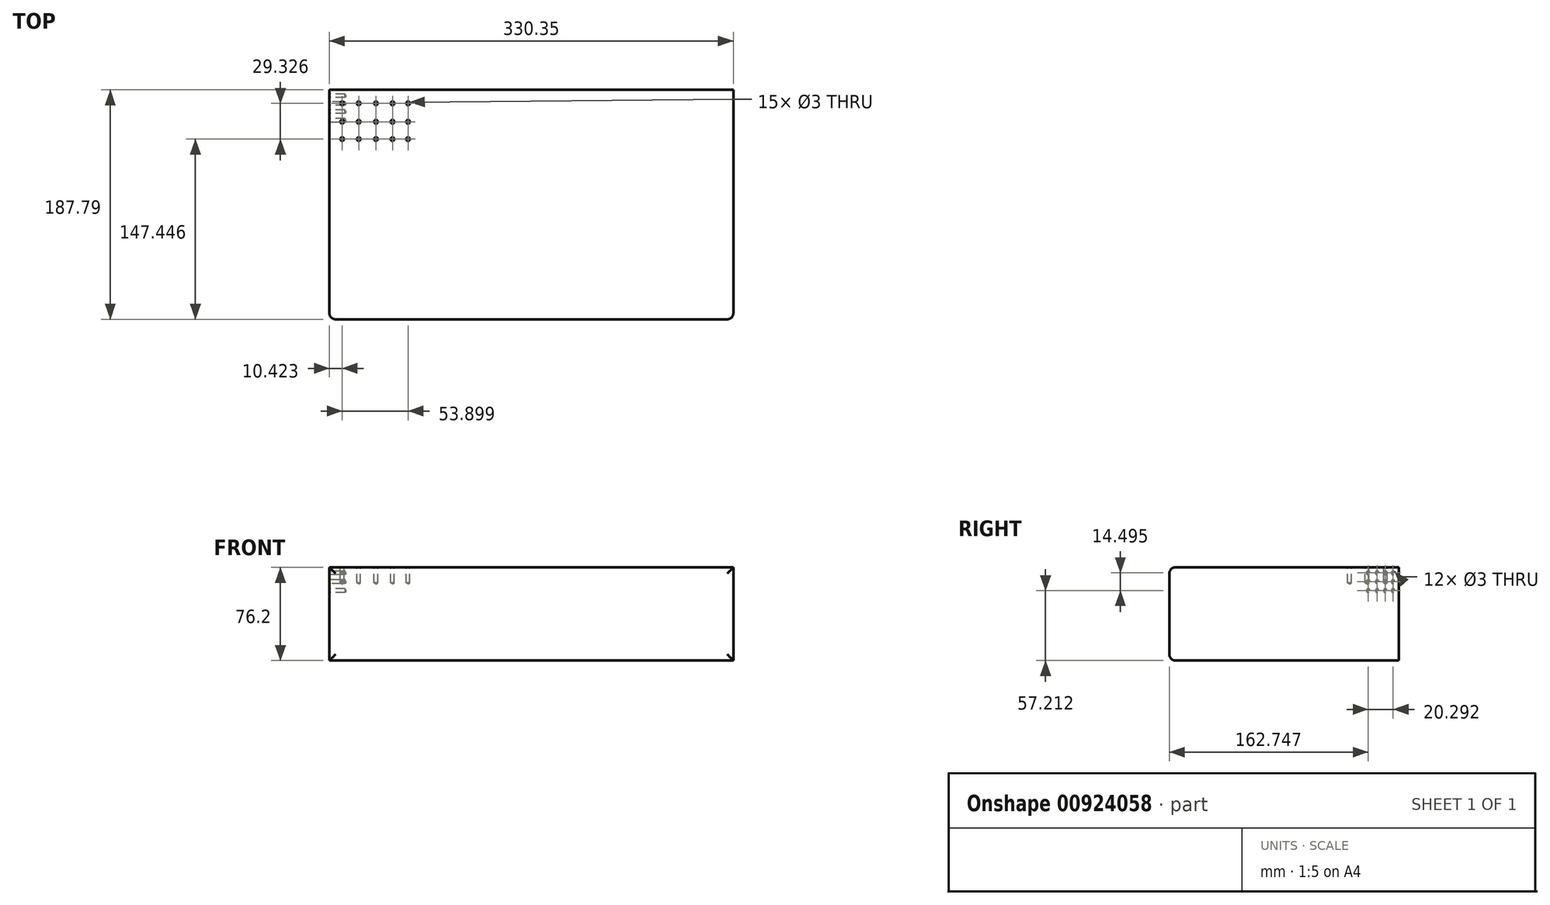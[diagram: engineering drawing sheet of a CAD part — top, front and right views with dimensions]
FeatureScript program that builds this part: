
annotation { "Feature Type Name" : "Feature", "Feature Type Description" : "" }
export const myFeature = defineFeature(function(context is Context, id is Id, definition is map)
    precondition{}
    {
        {
            var Q0;
            Q0=qCreatedBy(makeId("Top.planeOp"),FACE);
            var sketch = newSketch(context, id + "F0", { "sketchPlane" : qUnion([Q0])});
            skLineSegment(sketch, "E0.bottom", {"start": v(-154.54, 87.6) * mm, "end": v(175.81, 87.6) * mm});
            skLineSegment(sketch, "E0.top", {"start": v(-154.54, -100.2) * mm, "end": v(175.81, -100.2) * mm});
            skLineSegment(sketch, "E0.left", {"start": v(-154.54, 87.6) * mm, "end": v(-154.54, -100.2) * mm});
            skLineSegment(sketch, "E0.right", {"start": v(175.81, 87.6) * mm, "end": v(175.81, -100.2) * mm});
            skSolve(sketch);
        }
        {
            var Q0;
            Q0=makeQuery(id+"F0.imprint","IMPRINT",FACE,{"disambiguationData":[TD([[makeQuery(id+"F0.imprint","IMPRINT",EDGE,{"derivedFrom":sQuery(id+"F0.wireOp",EDGE,"E0.bottom")}),-1.0]])]});
            extrude(context, id + "F1", {"entities" : qUnion([Q0]), "oppositeDirection" : true, "depth" : 76.2 * mm, "offsetDistance" : 25.4 * mm});
        }
        {
            var Q0;
            Q0=makeQuery(id+"F1.opExtrude","CAP_EDGE",EDGE,{"disambiguationData":[OSD([sQuery(id+"F0.wireOp",EDGE,"E0.top")])],"isStart":true});
            var Q1;
            Q1=makeQuery(id+"F1.opExtrude","SWEPT_FACE",FACE,{"disambiguationData":[OSD([sQuery(id+"F0.wireOp",EDGE,"E0.top")])]});
            var Q2;
            Q2=makeQuery(id+"F1.opExtrude","CAP_EDGE",EDGE,{"disambiguationData":[OSD([sQuery(id+"F0.wireOp",EDGE,"E0.top")])],"isStart":false});
            fillet(context, id + "F2", {"entities" : qUnion([Q0, Q1, Q2]), "radius" : 5.08 * mm, "tangentPropagation" : true, "allowEdgeOverflow" : false});
        }
        {
            var Q0;
            Q0=makeQuery(id+"F1.opExtrude","CAP_FACE",FACE,{"disambiguationData":[OSD([sQuery(id+"F0.wireOp",EDGE,"E0.bottom"),sQuery(id+"F0.wireOp",EDGE,"E0.top"),sQuery(id+"F0.wireOp",EDGE,"E0.left"),sQuery(id+"F0.wireOp",EDGE,"E0.right")])],"isStart":true});
            var sketch = newSketch(context, id + "F3", { "sketchPlane" : qUnion([Q0])});
            skPoint(sketch, "E1", {"position": v(-144.12, 76.57) * mm});
            skPoint(sketch, "E2", {"position": v(-130.58, 76.57) * mm});
            skPoint(sketch, "E3", {"position": v(-130.58, 61.49) * mm});
            skPoint(sketch, "E4", {"position": v(-144.12, 61.49) * mm});
            skPoint(sketch, "E5", {"position": v(-144.12, 47.25) * mm});
            skPoint(sketch, "E6", {"position": v(-130.58, 47.25) * mm});
            skPoint(sketch, "E7", {"position": v(-116.47, 47.25) * mm});
            skPoint(sketch, "E8", {"position": v(-116.47, 61.49) * mm});
            skPoint(sketch, "E9", {"position": v(-116.47, 76.57) * mm});
            skPoint(sketch, "E10", {"position": v(-102.93, 47.25) * mm});
            skPoint(sketch, "E11", {"position": v(-102.93, 61.49) * mm});
            skPoint(sketch, "E12", {"position": v(-102.93, 76.57) * mm});
            skPoint(sketch, "E13", {"position": v(-90.22, 47.25) * mm});
            skPoint(sketch, "E14", {"position": v(-90.22, 61.49) * mm});
            skPoint(sketch, "E15", {"position": v(-90.22, 76.57) * mm});
            skSolve(sketch);
        }
        {
            var Q0;
            Q0=sQuery(id+"F3.wireOp",VERTEX,"E1");
            var Q1;
            Q1=sQuery(id+"F3.wireOp",VERTEX,"E4");
            var Q2;
            Q2=sQuery(id+"F3.wireOp",VERTEX,"E5");
            var Q3;
            Q3=sQuery(id+"F3.wireOp",VERTEX,"E6");
            var Q4;
            Q4=sQuery(id+"F3.wireOp",VERTEX,"E3");
            var Q5;
            Q5=sQuery(id+"F3.wireOp",VERTEX,"E2");
            var Q6;
            Q6=sQuery(id+"F3.wireOp",VERTEX,"E9");
            var Q7;
            Q7=sQuery(id+"F3.wireOp",VERTEX,"E8");
            var Q8;
            Q8=sQuery(id+"F3.wireOp",VERTEX,"E7");
            var Q9;
            Q9=sQuery(id+"F3.wireOp",VERTEX,"E10");
            var Q10;
            Q10=sQuery(id+"F3.wireOp",VERTEX,"E11");
            var Q11;
            Q11=sQuery(id+"F3.wireOp",VERTEX,"E12");
            var Q12;
            Q12=sQuery(id+"F3.wireOp",VERTEX,"E15");
            var Q13;
            Q13=sQuery(id+"F3.wireOp",VERTEX,"E14");
            var Q14;
            Q14=sQuery(id+"F3.wireOp",VERTEX,"E13");
            var Q15;
            Q15=makeQuery(id+"F1.opExtrude","SWEPT_BODY",BODY,{"disambiguationData":[OSD([sQuery(id+"F0.wireOp",EDGE,"E0.bottom"),sQuery(id+"F0.wireOp",EDGE,"E0.top"),sQuery(id+"F0.wireOp",EDGE,"E0.left"),sQuery(id+"F0.wireOp",EDGE,"E0.right")])]});
            hole(context, id + "F4", {"style" : HoleStyle.SIMPLE, "endStyle" : HoleEndStyle.BLIND, "standardTappedOrClearance" : lookupTablePath({ "standard" : "ISO", "size" : "3", "type" : "Drilled" }), "standardBlindInLast" : lookupTablePath({ "standard" : "ISO", "size" : "3", "type" : "Drilled" }), "holeDiameter" : 3 * mm, "majorDiameter" : 6.35 * mm, "holeDepth" : 12.7 * mm, "isTappedThrough" : true, "tappedDepth" : 12.7 * mm, "tapClearance" : 3, "locations" : qUnion([Q0, Q1, Q2, Q3, Q4, Q5, Q6, Q7, Q8, Q9, Q10, Q11, Q12, Q13, Q14]), "scope" : qUnion([Q15])});
        }
        {
            var Q0;
            Q0=makeQuery(id+"F1.opExtrude","SWEPT_FACE",FACE,{"disambiguationData":[OSD([sQuery(id+"F0.wireOp",EDGE,"E0.left")])]});
            var sketch = newSketch(context, id + "F5", { "sketchPlane" : qUnion([Q0])});
            skPoint(sketch, "E16", {"position": v(-82.84, -4.5) * mm});
            skPoint(sketch, "E17", {"position": v(-76.46, -4.5) * mm});
            skPoint(sketch, "E18", {"position": v(-69.8, -4.5) * mm});
            skPoint(sketch, "E19", {"position": v(-62.55, -4.5) * mm});
            skPoint(sketch, "E20", {"position": v(-62.55, -11.74) * mm});
            skPoint(sketch, "E21", {"position": v(-69.8, -11.74) * mm});
            skPoint(sketch, "E22", {"position": v(-76.46, -11.74) * mm});
            skPoint(sketch, "E23", {"position": v(-82.84, -11.74) * mm});
            skPoint(sketch, "E24", {"position": v(-82.84, -18.99) * mm});
            skPoint(sketch, "E25", {"position": v(-76.46, -18.99) * mm});
            skPoint(sketch, "E26", {"position": v(-69.8, -18.99) * mm});
            skPoint(sketch, "E27", {"position": v(-62.55, -18.99) * mm});
            skSolve(sketch);
        }
        {
            var Q0;
            Q0=sQuery(id+"F5.wireOp",VERTEX,"E16");
            var Q1;
            Q1=sQuery(id+"F5.wireOp",VERTEX,"E17");
            var Q2;
            Q2=sQuery(id+"F5.wireOp",VERTEX,"E18");
            var Q3;
            Q3=sQuery(id+"F5.wireOp",VERTEX,"E19");
            var Q4;
            Q4=sQuery(id+"F5.wireOp",VERTEX,"E20");
            var Q5;
            Q5=sQuery(id+"F5.wireOp",VERTEX,"E21");
            var Q6;
            Q6=sQuery(id+"F5.wireOp",VERTEX,"E22");
            var Q7;
            Q7=sQuery(id+"F5.wireOp",VERTEX,"E23");
            var Q8;
            Q8=sQuery(id+"F5.wireOp",VERTEX,"E24");
            var Q9;
            Q9=sQuery(id+"F5.wireOp",VERTEX,"E25");
            var Q10;
            Q10=sQuery(id+"F5.wireOp",VERTEX,"E26");
            var Q11;
            Q11=sQuery(id+"F5.wireOp",VERTEX,"E27");
            var Q12;
            Q12=makeQuery(id+"F1.opExtrude","SWEPT_BODY",BODY,{"disambiguationData":[OSD([sQuery(id+"F0.wireOp",EDGE,"E0.bottom"),sQuery(id+"F0.wireOp",EDGE,"E0.top"),sQuery(id+"F0.wireOp",EDGE,"E0.left"),sQuery(id+"F0.wireOp",EDGE,"E0.right")])]});
            hole(context, id + "F6", {"style" : HoleStyle.SIMPLE, "endStyle" : HoleEndStyle.BLIND, "standardTappedOrClearance" : lookupTablePath({ "standard" : "ISO", "size" : "3", "type" : "Drilled" }), "standardBlindInLast" : lookupTablePath({ "standard" : "ISO", "size" : "3", "type" : "Drilled" }), "holeDiameter" : 3 * mm, "majorDiameter" : 6.35 * mm, "holeDepth" : 12.7 * mm, "isTappedThrough" : true, "tappedDepth" : 12.7 * mm, "tapClearance" : 3, "locations" : qUnion([Q0, Q1, Q2, Q3, Q4, Q5, Q6, Q7, Q8, Q9, Q10, Q11]), "scope" : qUnion([Q12])});
        }
    });
